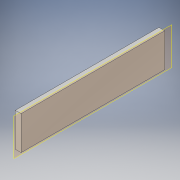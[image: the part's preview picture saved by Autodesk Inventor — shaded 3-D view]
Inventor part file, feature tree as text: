
AUTODESK INVENTOR PART (.ipt)
format: ipt  version: 2018 (Build 220112000, 112)  size: 93,184 bytes
history: native  units: in
note: dims shown in document units (in); Inventor stores cm internally (conversion verified against a paired STEP export)
features: extrude x1, sketch x1
ambient origin geometry x8: Origin, YZ Plane, XZ Plane, XY Plane, X Axis, Y Axis, Z Axis, Center Point
bodies: Solid1 (feature_tree)
feature tree (2):
  extrude  "Extrusion1"  Depth=5.8661in
  sketch  "Sketch1"  dims[d0=1.378in d1=5.8661in d2=0.2362in d3=0.0in]
